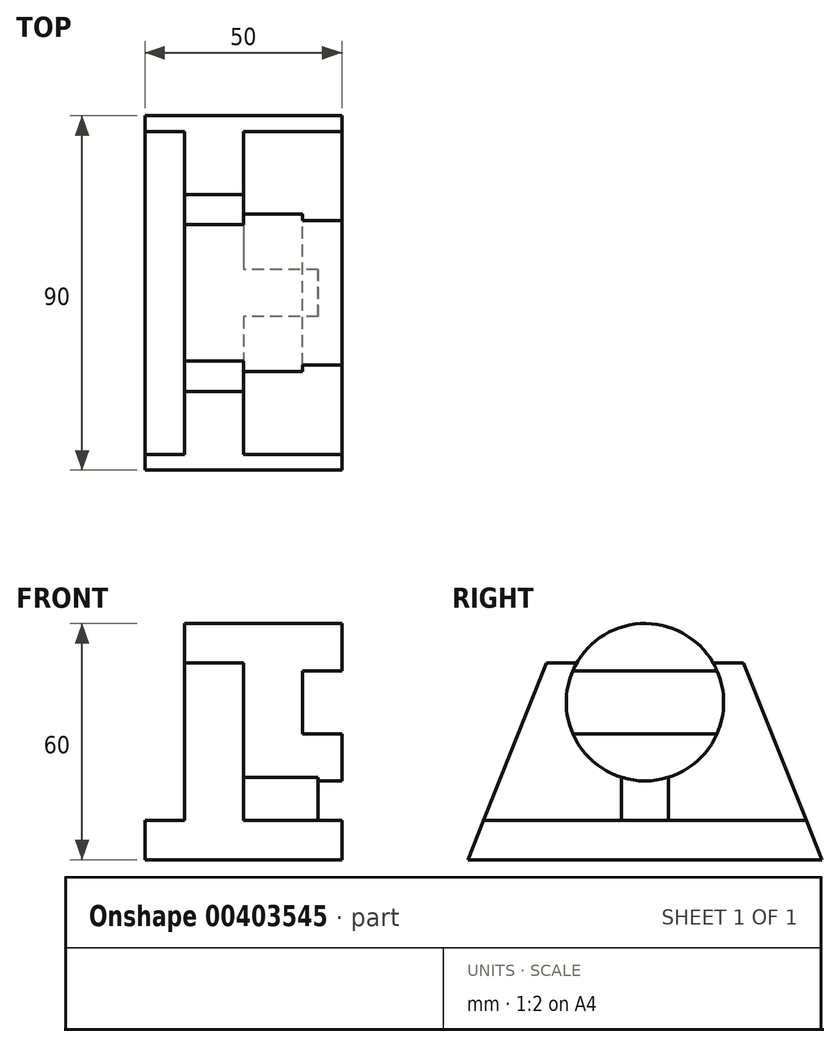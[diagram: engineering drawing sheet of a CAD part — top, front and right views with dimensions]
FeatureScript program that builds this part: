
annotation { "Feature Type Name" : "Feature", "Feature Type Description" : "" }
export const myFeature = defineFeature(function(context is Context, id is Id, definition is map)
    precondition{}
    {
        {
            var Q0;
            Q0=qCreatedBy(makeId("Right.planeOp"),FACE);
            var sketch = newSketch(context, id + "F0", { "sketchPlane" : qUnion([Q0])});
            skLineSegment(sketch, "E0", {"start": v(0, 0) * mm, "end": v(45, 0) * mm});
            skLineSegment(sketch, "E1", {"start": v(45, 0) * mm, "end": v(25, 50) * mm});
            skLineSegment(sketch, "E2", {"start": v(25, 50) * mm, "end": v(0, 50) * mm});
            skLineSegment(sketch, "E3", {"start": v(0, 50) * mm, "end": v(0, 0) * mm, "construction": true});
            skLineSegment(sketch, "E4.MirrorCS", {"start": v(-25, 50) * mm, "end": v(0, 50) * mm});
            skLineSegment(sketch, "E5.MirrorCS", {"start": v(-45, 0) * mm, "end": v(-25, 50) * mm});
            skLineSegment(sketch, "E6.MirrorCS", {"start": v(0, 0) * mm, "end": v(-45, 0) * mm});
            skSolve(sketch);
        }
        {
            var Q0;
            Q0 = qSketchRegion(id + "F0", true);
            extrude(context, id + "F1", {"entities" : qUnion([Q0]), "oppositeDirection" : true, "depth" : 50 * mm});
        }
        {
            var Q0;
            Q0=qCreatedBy(makeId("Front.planeOp"),FACE);
            var sketch = newSketch(context, id + "F2", { "sketchPlane" : qUnion([Q0])});
            skLineSegment(sketch, "E7.bottom", {"start": v(0, 50) * mm, "end": v(-25, 50) * mm});
            skLineSegment(sketch, "E7.top", {"start": v(0, 10) * mm, "end": v(-25, 10) * mm});
            skLineSegment(sketch, "E7.left", {"start": v(0, 50) * mm, "end": v(0, 10) * mm});
            skLineSegment(sketch, "E7.right", {"start": v(-25, 50) * mm, "end": v(-25, 10) * mm});
            skLineSegment(sketch, "E8.bottom", {"start": v(-50, 50) * mm, "end": v(-40, 50) * mm});
            skLineSegment(sketch, "E8.top", {"start": v(-50, 10) * mm, "end": v(-40, 10) * mm});
            skLineSegment(sketch, "E8.left", {"start": v(-50, 50) * mm, "end": v(-50, 10) * mm});
            skLineSegment(sketch, "E8.right", {"start": v(-40, 50) * mm, "end": v(-40, 10) * mm});
            skSolve(sketch);
        }
        {
            var Q0;
            Q0 = qSketchRegion(id + "F2", true);
            extrude(context, id + "F3", {"entities" : qUnion([Q0]), "operationType" : NewBodyOperationType.REMOVE, "endBound" : BoundingType.THROUGH_ALL, "oppositeDirection" : true, "depth" : 25 * mm, "hasSecondDirection" : true, "secondDirectionBound" : SecondDirectionBoundingType.THROUGH_ALL, "secondDirectionOppositeDirection" : false, "secondDirectionDepth" : 25 * mm});
        }
        {
            var Q0;
            Q0=makeQuery(id+"F3.boolean.opBoolean","COPY",FACE,{"derivedFrom":makeQuery(id+"F3.opExtrude","SWEPT_FACE",FACE,{"disambiguationData":[OSD([sQuery(id+"F2.wireOp",EDGE,"E8.right")])]})});
            var sketch = newSketch(context, id + "F4", { "sketchPlane" : qUnion([Q0])});
            skCircle(sketch, "E9", {"center": v(0, 40) * mm, "radius": 20 * mm});
            skSolve(sketch);
        }
        {
            var Q0;
            Q0 = qSketchRegion(id + "F4", true);
            extrude(context, id + "F5", {"entities" : qUnion([Q0]), "operationType" : NewBodyOperationType.ADD, "oppositeDirection" : true, "depth" : 40 * mm});
        }
        {
            var Q0;
            Q0=makeQuery(id+"F3.boolean.opBoolean","COPY",FACE,{"derivedFrom":makeQuery(id+"F3.opExtrude","SWEPT_FACE",FACE,{"disambiguationData":[OSD([sQuery(id+"F2.wireOp",EDGE,"E7.right")])]})});
            var sketch = newSketch(context, id + "F6", { "sketchPlane" : qUnion([Q0])});
            skLineSegment(sketch, "E10.bottom", {"start": v(-6, 22) * mm, "end": v(6, 22) * mm});
            skLineSegment(sketch, "E10.top", {"start": v(-6, 10) * mm, "end": v(6, 10) * mm});
            skLineSegment(sketch, "E10.left", {"start": v(-6, 22) * mm, "end": v(-6, 10) * mm});
            skLineSegment(sketch, "E10.right", {"start": v(6, 22) * mm, "end": v(6, 10) * mm});
            skCircle(sketch, "E11.0", {"center": v(0, 40) * mm, "radius": 20 * mm, "construction": true});
            skLineSegment(sketch, "E12", {"start": v(0, 40) * mm, "end": v(0, 16.96) * mm, "construction": true});
            skPoint(sketch, "E12.endSnap0", {"position": v(0, 20) * mm});
            skLineSegment(sketch, "E13", {"start": v(0, 22) * mm, "end": v(0, 10) * mm, "construction": true});
            skSolve(sketch);
        }
        {
            var Q0;
            Q0 = qSketchRegion(id + "F6", true);
            extrude(context, id + "F7", {"entities" : qUnion([Q0]), "operationType" : NewBodyOperationType.ADD, "depth" : 19 * mm});
        }
        {
            var Q0;
            Q0=makeQuery(id+"F5.opExtrude","CAP_FACE",FACE,{"disambiguationData":[OSD([sQuery(id+"F4.wireOp",EDGE,"E9")])],"isStart":false});
            var sketch = newSketch(context, id + "F8", { "sketchPlane" : qUnion([Q0])});
            skCircle(sketch, "E14.0", {"center": v(0, 40) * mm, "radius": 20 * mm, "construction": true});
            skLineSegment(sketch, "E15", {"start": v(0, 40) * mm, "end": v(-20, 40) * mm, "construction": true});
            skLineSegment(sketch, "E16", {"start": v(0, 40) * mm, "end": v(0, 60) * mm, "construction": true});
            skLineSegment(sketch, "E17.bottom", {"start": v(-20, 48) * mm, "end": v(20, 48) * mm});
            skLineSegment(sketch, "E17.top", {"start": v(-20, 32) * mm, "end": v(20, 32) * mm});
            skLineSegment(sketch, "E17.left", {"start": v(-20, 48) * mm, "end": v(-20, 32) * mm});
            skLineSegment(sketch, "E17.right", {"start": v(20, 48) * mm, "end": v(20, 32) * mm});
            skSolve(sketch);
        }
        {
            var Q0;
            Q0 = qSketchRegion(id + "F8", true);
            extrude(context, id + "F9", {"entities" : qUnion([Q0]), "operationType" : NewBodyOperationType.REMOVE, "oppositeDirection" : true, "depth" : 10 * mm});
        }
    });
